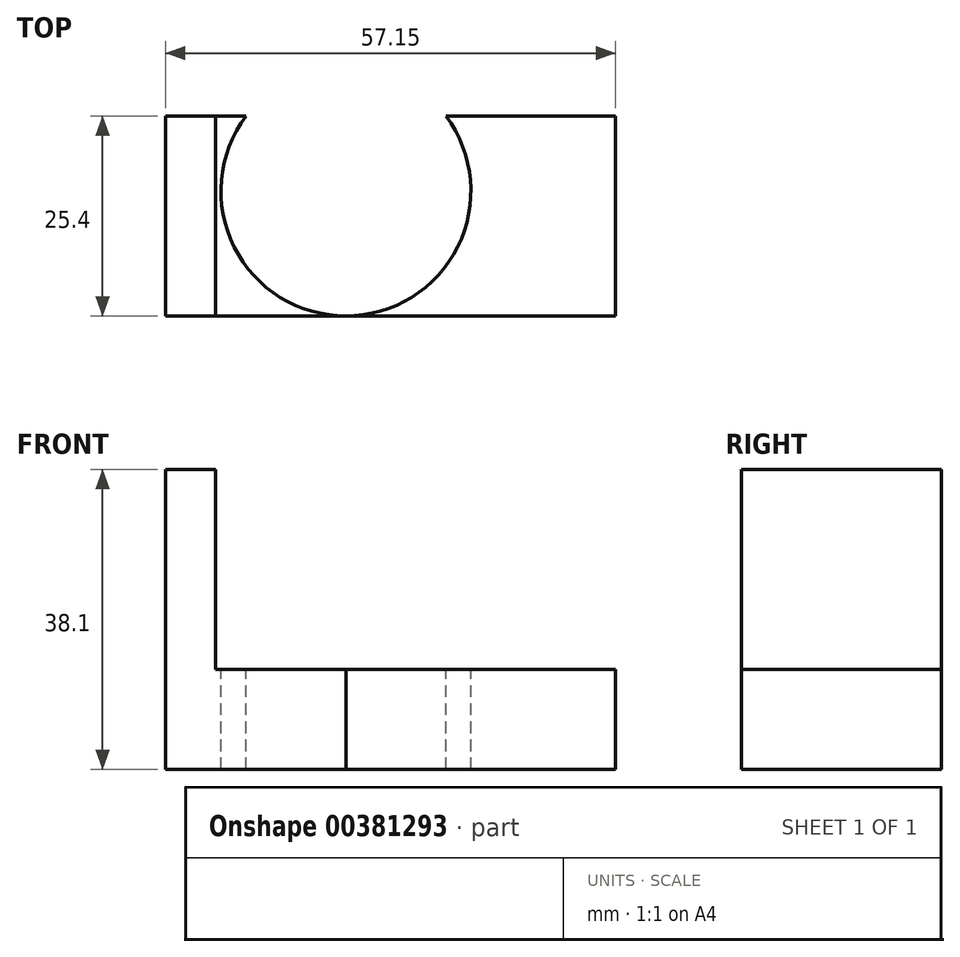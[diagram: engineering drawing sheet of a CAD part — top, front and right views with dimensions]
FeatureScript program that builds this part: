
annotation { "Feature Type Name" : "Feature", "Feature Type Description" : "" }
export const myFeature = defineFeature(function(context is Context, id is Id, definition is map)
    precondition{}
    {
        {
            var Q0;
            Q0=qCreatedBy(makeId("Front.planeOp"),FACE);
            var sketch = newSketch(context, id + "F0", { "sketchPlane" : qUnion([Q0])});
            skLineSegment(sketch, "E0", {"start": v(0, 0) * mm, "end": v(0, 38.1) * mm});
            skLineSegment(sketch, "E1", {"start": v(0, 38.1) * mm, "end": v(6.35, 38.1) * mm});
            skLineSegment(sketch, "E2", {"start": v(6.35, 38.1) * mm, "end": v(6.35, 12.7) * mm});
            skLineSegment(sketch, "E3", {"start": v(6.35, 12.7) * mm, "end": v(57.15, 12.7) * mm});
            skLineSegment(sketch, "E4", {"start": v(57.15, 12.7) * mm, "end": v(57.15, 0) * mm});
            skLineSegment(sketch, "E5", {"start": v(57.15, 0) * mm, "end": v(0, 0) * mm});
            skSolve(sketch);
        }
        {
            var Q0;
            Q0 = qSketchRegion(id + "F0", true);
            extrude(context, id + "F1", {"entities" : qUnion([Q0]), "depth" : 25.4 * mm});
        }
        {
            var Q0;
            Q0=makeQuery(id+"F1.opExtrude","SWEPT_FACE",FACE,{"disambiguationData":[OSD([sQuery(id+"F0.wireOp",EDGE,"E3")])]});
            var sketch = newSketch(context, id + "F2", { "sketchPlane" : qUnion([Q0])});
            skCircle(sketch, "E6", {"center": v(22.9, -9.52) * mm, "radius": 15.88 * mm});
            skSolve(sketch);
        }
        {
            var Q0;
            {var subQ0=sQuery(id+"F2.wireOp",EDGE,"E6");var subQ1=sQuery(id+"F0.wireOp",EDGE,"E3");var subQ2=makeQuery(id+"F1.opExtrude","CAP_EDGE",EDGE,{"disambiguationData":[OSD([subQ1])],"isStart":true});var subQ3=makeQuery(id+"F2.imprint","INTERSECT",VERTEX,{"disambiguationData":[OD(0.0)],"derivedFrom":[subQ2,subQ0]});Q0=makeQuery(id+"F2.imprint","IMPRINT",FACE,{"disambiguationData":[TD([[makeQuery(id+"F2.imprint","IMPRINT",EDGE,{"disambiguationData":[TD([[subQ3,-1.0]])],"derivedFrom":subQ0}),1.0]])]});}
            extrude(context, id + "F3", {"entities" : qUnion([Q0]), "operationType" : NewBodyOperationType.REMOVE, "oppositeDirection" : true, "depth" : 25.4 * mm});
        }
    });
